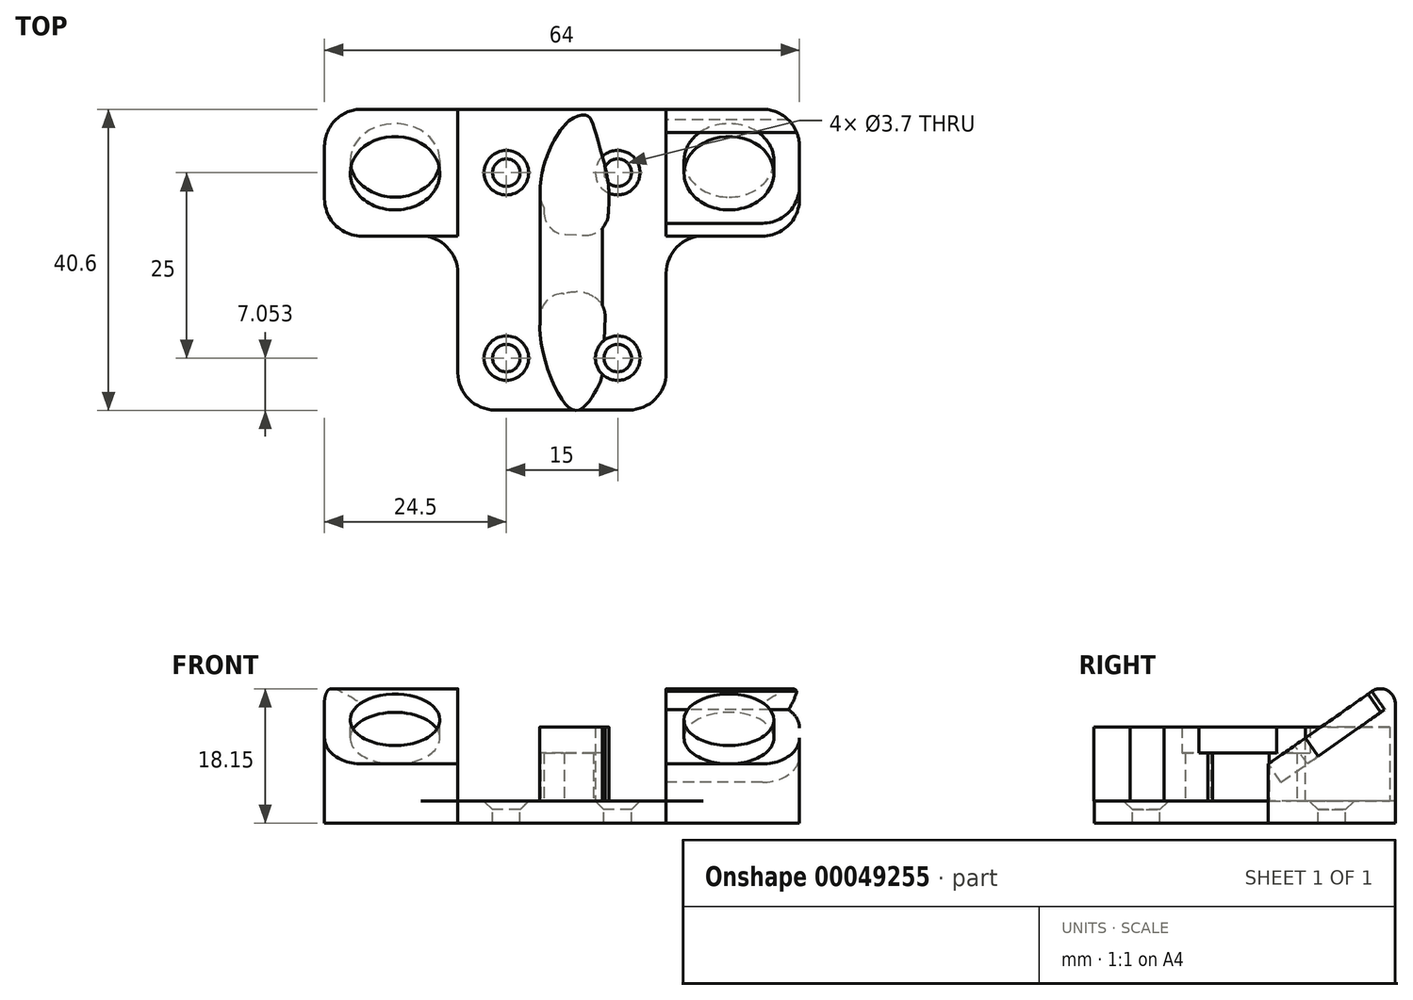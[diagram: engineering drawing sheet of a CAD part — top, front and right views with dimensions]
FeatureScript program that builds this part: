
annotation { "Feature Type Name" : "Feature", "Feature Type Description" : "" }
export const myFeature = defineFeature(function(context is Context, id is Id, definition is map)
    precondition{}
    {
        {
            var Q0;
            Q0=qCreatedBy(makeId("Top.planeOp"),FACE);
            var sketch = newSketch(context, id + "F0", { "sketchPlane" : qUnion([Q0])});
            skLineSegment(sketch, "E0.rect.top", {"start": v(-9.03, -25.17) * mm, "end": v(9.03, -25.17) * mm});
            skPoint(sketch, "E0.rect.middle", {"position": v(0, 0) * mm});
            skLineSegment(sketch, "E1.rect.bottom", {"start": v(27, 15.36) * mm, "end": v(-27, 15.36) * mm});
            skLineSegment(sketch, "E1.rect.top", {"start": v(27, -1.74) * mm, "end": v(19.03, -1.74) * mm});
            skLineSegment(sketch, "E1.rect.left", {"start": v(32, 15.36) * mm, "end": v(32, 15.36) * mm});
            skLineSegment(sketch, "E1.rect.right", {"start": v(-32, 10.36) * mm, "end": v(-32, 3.26) * mm});
            skPoint(sketch, "E1.rect.middle", {"position": v(0, 6.81) * mm});
            skLineSegment(sketch, "E2.trimOffspring", {"start": v(-19.03, -1.74) * mm, "end": v(-27, -1.74) * mm});
            skLineSegment(sketch, "E3", {"start": v(0, 6.81) * mm, "end": v(0, -18.19) * mm, "construction": true});
            skPoint(sketch, "E3.endSnap0", {"position": v(0, -25.17) * mm});
            skLineSegment(sketch, "E4", {"start": v(0, 6.81) * mm, "end": v(32, 6.81) * mm, "construction": true});
            skLineSegment(sketch, "E5", {"start": v(0, 6.81) * mm, "end": v(-32, 6.81) * mm, "construction": true});
            skPoint(sketch, "E6", {"position": v(7.5, 6.81) * mm});
            skLineSegment(sketch, "E7", {"start": v(7.5, 6.81) * mm, "end": v(7.5, -18.19) * mm, "construction": true});
            skPoint(sketch, "E8", {"position": v(7.5, -18.19) * mm});
            skPoint(sketch, "E9.MirrorP", {"position": v(-7.5, -18.19) * mm});
            skPoint(sketch, "E10.MirrorP", {"position": v(-7.5, 6.81) * mm});
            skCircle(sketch, "E11", {"center": v(-22.5, 6.81) * mm, "radius": 6.05 * mm, "construction": true});
            skCircle(sketch, "E12", {"center": v(22.5, 6.72) * mm, "radius": 6.05 * mm, "construction": true});
            skLineSegment(sketch, "E13", {"start": v(-7.5, 6.81) * mm, "end": v(-7.5, -18.19) * mm, "construction": true});
            skLineSegment(sketch, "E14", {"start": v(-7.5, -18.19) * mm, "end": v(7.5, -18.19) * mm, "construction": true});
            skPoint(sketch, "E15.orphan", {"position": v(0, -14.27) * mm});
            skPoint(sketch, "E16.orphan", {"position": v(0, 15.36) * mm});
            skLineSegment(sketch, "E17", {"start": v(14.03, -20.17) * mm, "end": v(14.03, -6.74) * mm});
            skLineSegment(sketch, "E18.MirrorCS", {"start": v(-14.03, -20.17) * mm, "end": v(-14.03, -6.74) * mm});
            skPoint(sketch, "E19.orphan", {"position": v(18, -25.17) * mm});
            skPoint(sketch, "E20.orphan", {"position": v(-18, -25.17) * mm});
            skLineSegment(sketch, "E21", {"start": v(14.03, -6.74) * mm, "end": v(14.03, 15.36) * mm});
            skLineSegment(sketch, "E22", {"start": v(32, -1.74) * mm, "end": v(32, -1.74) * mm});
            skLineSegment(sketch, "E23", {"start": v(32, 10.36) * mm, "end": v(32, 3.26) * mm});
            skLineSegment(sketch, "E24", {"start": v(14.03, 15.36) * mm, "end": v(14.03, 15.36) * mm});
            skLineSegment(sketch, "E25", {"start": v(-14.03, 15.36) * mm, "end": v(-14.03, 15.36) * mm});
            skLineSegment(sketch, "E26", {"start": v(-14.03, -6.74) * mm, "end": v(-14.03, 15.36) * mm});
            skLineSegment(sketch, "E27", {"start": v(-32, -1.74) * mm, "end": v(-32, -1.74) * mm});
            skLineSegment(sketch, "E28", {"start": v(-32, 15.36) * mm, "end": v(-32, 15.36) * mm});
            skArc(sketch, "E29.filletArc", {"start": v(19.03, -1.74) * mm, "mid": v(15.5, -3.2) * mm, "end": v(14.03, -6.74) * mm});
            skArc(sketch, "E30.filletArc", {"start": v(-14.03, -6.74) * mm, "mid": v(-15.5, -3.2) * mm, "end": v(-19.03, -1.74) * mm});
            skPoint(sketch, "E31.visualSharp", {"position": v(-14.03, -25.17) * mm});
            skArc(sketch, "E31.filletArc", {"start": v(-14.03, -20.17) * mm, "mid": v(-12.57, -23.7) * mm, "end": v(-9.03, -25.17) * mm});
            skPoint(sketch, "E32.visualSharp", {"position": v(14.03, -25.17) * mm});
            skArc(sketch, "E32.filletArc", {"start": v(9.03, -25.17) * mm, "mid": v(12.57, -23.7) * mm, "end": v(14.03, -20.17) * mm});
            skPoint(sketch, "E33.visualSharp", {"position": v(32, -1.74) * mm});
            skArc(sketch, "E33.filletArc", {"start": v(27, -1.74) * mm, "mid": v(30.54, -0.27) * mm, "end": v(32, 3.26) * mm});
            skPoint(sketch, "E34.visualSharp", {"position": v(32, 15.36) * mm});
            skArc(sketch, "E34.filletArc", {"start": v(32, 10.36) * mm, "mid": v(30.54, 13.9) * mm, "end": v(27, 15.36) * mm});
            skPoint(sketch, "E35.visualSharp", {"position": v(-32, 15.36) * mm});
            skArc(sketch, "E35.filletArc", {"start": v(-27, 15.36) * mm, "mid": v(-30.54, 13.9) * mm, "end": v(-32, 10.36) * mm});
            skPoint(sketch, "E36.visualSharp", {"position": v(-32, -1.74) * mm});
            skArc(sketch, "E36.filletArc", {"start": v(-32, 3.26) * mm, "mid": v(-30.54, -0.27) * mm, "end": v(-27, -1.74) * mm});
            skPoint(sketch, "E37.orphan", {"position": v(-14.03, -4.9) * mm});
            skPoint(sketch, "E38.orphan", {"position": v(14.03, -4.9) * mm});
            skLineSegment(sketch, "E39", {"start": v(-20.86, -1.74) * mm, "end": v(21.69, -1.74) * mm});
            skSolve(sketch);
        }
        {
            var Q0;
            Q0=makeQuery(id+"F0.imprint","IMPRINT",FACE,{"disambiguationData":[TD([[makeQuery(id+"F0.imprint","IMPRINT",EDGE,{"derivedFrom":sQuery(id+"F0.wireOp",EDGE,"E1.rect.right")}),1.0]])]});
            var Q1;
            Q1=makeQuery(id+"F0.imprint","IMPRINT",FACE,{"disambiguationData":[TD([[makeQuery(id+"F0.imprint","IMPRINT",EDGE,{"derivedFrom":sQuery(id+"F0.wireOp",EDGE,"E0.rect.top")}),1.0]])]});
            var Q2;
            Q2=makeQuery(id+"F0.imprint","IMPRINT",FACE,{"disambiguationData":[TD([[makeQuery(id+"F0.imprint","IMPRINT",EDGE,{"derivedFrom":sQuery(id+"F0.wireOp",EDGE,"E1.rect.top")}),-1.0]])]});
            var Q3;
            {var subQ0=sQuery(id+"F0.wireOp",EDGE,"E21");var subQ1=sQuery(id+"F0.wireOp",EDGE,"E1.rect.bottom");var subQ2=makeQuery(id+"F0.imprint","INTERSECT",VERTEX,{"derivedFrom":[subQ1,subQ0]});Q3=makeQuery(id+"F0.imprint","IMPRINT",FACE,{"disambiguationData":[TD([[makeQuery(id+"F0.imprint","IMPRINT",EDGE,{"disambiguationData":[TD([[subQ2,-1.0]])],"derivedFrom":subQ1}),1.0]])]});}
            var Q4;
            {var subQ0=sQuery(id+"F0.wireOp",EDGE,"E30.filletArc");Q4=makeQuery(id+"F0.imprint","IMPRINT",FACE,{"disambiguationData":[TD([[makeQuery(id+"F0.imprint","IMPRINT",EDGE,{"derivedFrom":subQ0}),-1.0]])]});}
            var Q5;
            {var subQ0=sQuery(id+"F0.wireOp",EDGE,"E29.filletArc");Q5=makeQuery(id+"F0.imprint","IMPRINT",FACE,{"disambiguationData":[TD([[makeQuery(id+"F0.imprint","IMPRINT",EDGE,{"derivedFrom":subQ0}),-1.0]])]});}
            extrude(context, id + "F1", {"entities" : qUnion([Q0, Q1, Q2, Q3, Q4, Q5]), "depth" : 3 * mm});
        }
        {
            var Q0;
            Q0=qCreatedBy(makeId("Right.planeOp"),FACE);
            var sketch = newSketch(context, id + "F2", { "sketchPlane" : qUnion([Q0])});
            skLineSegment(sketch, "E40.0", {"start": v(-1.74, 3) * mm, "end": v(-1.74, 0) * mm});
            skLineSegment(sketch, "E41.0", {"start": v(15.36, 3) * mm, "end": v(15.36, 0) * mm});
            skLineSegment(sketch, "E42", {"start": v(-1.74, 3) * mm, "end": v(15.36, 3) * mm});
            skLineSegment(sketch, "E43", {"start": v(15.36, 3) * mm, "end": v(15.36, 16.15) * mm});
            skLineSegment(sketch, "E44", {"start": v(-1.74, 3) * mm, "end": v(-1.74, 8) * mm});
            skLineSegment(sketch, "E45", {"start": v(-1.74, 8) * mm, "end": v(12.22, 17.8) * mm});
            skPoint(sketch, "E46.visualSharp", {"position": v(15.36, 20) * mm});
            skArc(sketch, "E46.filletArc", {"start": v(15.36, 16.15) * mm, "mid": v(14.29, 17.93) * mm, "end": v(12.22, 17.8) * mm});
            skSolve(sketch);
        }
        {
            var Q0;
            Q0=makeQuery(id+"F2.imprint","IMPRINT",FACE,{"disambiguationData":[TD([[makeQuery(id+"F2.imprint","IMPRINT",EDGE,{"derivedFrom":sQuery(id+"F2.wireOp",EDGE,"E42")}),1.0]])]});
            var Q1;
            Q1=makeQuery(id+"F1.opExtrude","SWEPT_FACE",FACE,{"disambiguationData":[OSD([sQuery(id+"F0.wireOp",EDGE,"E23")])]});
            var Q2;
            Q2=makeQuery(id+"F1.opExtrude","SWEPT_FACE",FACE,{"disambiguationData":[OSD([sQuery(id+"F0.wireOp",EDGE,"E1.rect.right")])]});
            extrude(context, id + "F3", {"entities" : qUnion([Q0]), "operationType" : NewBodyOperationType.ADD, "endBound" : BoundingType.UP_TO_SURFACE, "endBoundEntityFace" : qUnion([Q1]), "depth" : 25 * mm, "hasSecondDirection" : true, "secondDirectionBound" : SecondDirectionBoundingType.UP_TO_SURFACE, "secondDirectionOppositeDirection" : true, "secondDirectionBoundEntityFace" : qUnion([Q2]), "secondDirectionDepth" : 25 * mm});
        }
        {
            var Q0;
            {var subQ1=sQuery(id+"F2.wireOp",EDGE,"E42");Q0=makeQuery(id+"F3.boolean.opBoolean","SPLIT",FACE,{"disambiguationData":[TD([makeQuery(id+"F1.opExtrude","SWEPT_FACE",FACE,{"disambiguationData":[OSD([sQuery(id+"F0.wireOp",EDGE,"E35.filletArc")])]})])],"derivedFrom":makeQuery(id+"F3.opExtrude","SWEPT_FACE",FACE,{"disambiguationData":[OSD([subQ1])]})});}
            var Q1;
            {var subQ2=sQuery(id+"F2.wireOp",EDGE,"E42");Q1=makeQuery(id+"F3.boolean.opBoolean","SPLIT",FACE,{"disambiguationData":[TD([makeQuery(id+"F1.opExtrude","SWEPT_FACE",FACE,{"disambiguationData":[OSD([sQuery(id+"F0.wireOp",EDGE,"E36.filletArc")])]})])],"derivedFrom":makeQuery(id+"F3.opExtrude","SWEPT_FACE",FACE,{"disambiguationData":[OSD([subQ2])]})});}
            var Q2;
            {var subQ2=sQuery(id+"F2.wireOp",EDGE,"E42");Q2=makeQuery(id+"F3.boolean.opBoolean","SPLIT",FACE,{"disambiguationData":[TD([makeQuery(id+"F1.opExtrude","SWEPT_FACE",FACE,{"disambiguationData":[OSD([sQuery(id+"F0.wireOp",EDGE,"E33.filletArc")])]})])],"derivedFrom":makeQuery(id+"F3.opExtrude","SWEPT_FACE",FACE,{"disambiguationData":[OSD([subQ2])]})});}
            var Q3;
            {var subQ1=sQuery(id+"F2.wireOp",EDGE,"E42");Q3=makeQuery(id+"F3.boolean.opBoolean","SPLIT",FACE,{"disambiguationData":[TD([makeQuery(id+"F1.opExtrude","SWEPT_FACE",FACE,{"disambiguationData":[OSD([sQuery(id+"F0.wireOp",EDGE,"E34.filletArc")])]})])],"derivedFrom":makeQuery(id+"F3.opExtrude","SWEPT_FACE",FACE,{"disambiguationData":[OSD([subQ1])]})});}
            extrude(context, id + "F4", {"entities" : qUnion([Q0, Q1, Q2, Q3]), "operationType" : NewBodyOperationType.REMOVE, "oppositeDirection" : true, "depth" : 25 * mm});
        }
        {
            var Q0;
            Q0=makeQuery(id+"F3.opExtrude","SWEPT_FACE",FACE,{"disambiguationData":[OSD([sQuery(id+"F2.wireOp",EDGE,"E45")])]});
            var sketch = newSketch(context, id + "F5", { "sketchPlane" : qUnion([Q0])});
            skCircle(sketch, "E47", {"center": v(-22.5, 13.54) * mm, "radius": 6.05 * mm});
            skLineSegment(sketch, "E48.0", {"start": v(0, 23.81) * mm, "end": v(0, -14.89) * mm, "construction": true});
            skPoint(sketch, "E49.orphan", {"position": v(0, 5.58) * mm});
            skCircle(sketch, "E50.MirrorC", {"center": v(22.5, 13.54) * mm, "radius": 6.05 * mm});
            skLineSegment(sketch, "E51.0", {"start": v(14.03, 0) * mm, "end": v(14.03, 28.57) * mm});
            skLineSegment(sketch, "E52.0", {"start": v(-14.03, 0) * mm, "end": v(-14.03, 28.57) * mm});
            skPoint(sketch, "E53.orphan", {"position": v(-14.03, 12.58) * mm});
            skPoint(sketch, "E54.orphan", {"position": v(14.03, 12.58) * mm});
            skLineSegment(sketch, "E55", {"start": v(-14.03, 28.57) * mm, "end": v(14.09, 28.57) * mm});
            skPoint(sketch, "E56.orphan", {"position": v(14.03, -5.52) * mm});
            skPoint(sketch, "E57.orphan", {"position": v(-14.03, -5.52) * mm});
            skLineSegment(sketch, "E58", {"start": v(14.03, 0) * mm, "end": v(14.03, -5.02) * mm});
            skLineSegment(sketch, "E59", {"start": v(14.03, -5.02) * mm, "end": v(-14.03, -5.02) * mm});
            skLineSegment(sketch, "E60", {"start": v(-14.03, 0) * mm, "end": v(-14.03, -5.02) * mm});
            skSolve(sketch);
        }
        {
            var Q0;
            {var subQ0=sQuery(id+"F5.wireOp",EDGE,"E51.0");var subQ1=makeQuery(id+"F2.imprint","IMPRINT",EDGE,{"derivedFrom":sQuery(id+"F2.wireOp",EDGE,"E45")});var subQ2=makeQuery(id+"F3.opExtrude","TWEAK_EDGE",EDGE,{"derivedFrom":[makeQuery(id+"F2.imprint","IMPRINT",EDGE,{"derivedFrom":sQuery(id+"F2.wireOp",EDGE,"E44")}),subQ1]});var subQ3=makeQuery(id+"F5.imprint","INTERSECT",VERTEX,{"derivedFrom":[subQ2,subQ0]});Q0=makeQuery(id+"F5.imprint","IMPRINT",FACE,{"disambiguationData":[TD([[makeQuery(id+"F5.imprint","IMPRINT",EDGE,{"disambiguationData":[TD([[subQ3,-1.0]])],"derivedFrom":subQ0}),1.0]])]});}
            var Q1;
            {var subQ0=sQuery(id+"F5.wireOp",EDGE,"E58");Q1=makeQuery(id+"F5.imprint","IMPRINT",FACE,{"disambiguationData":[TD([[makeQuery(id+"F5.imprint","IMPRINT",EDGE,{"derivedFrom":subQ0}),-1.0]])]});}
            var Q2;
            {var subQ0=sQuery(id+"F5.wireOp",EDGE,"E55");var subQ1=sQuery(id+"F5.wireOp",EDGE,"E51.0");var subQ2=makeQuery(id+"F5.imprint","INTERSECT",VERTEX,{"derivedFrom":[subQ1,subQ0]});Q2=makeQuery(id+"F5.imprint","IMPRINT",FACE,{"disambiguationData":[TD([[makeQuery(id+"F5.imprint","IMPRINT",EDGE,{"disambiguationData":[TD([[subQ2,1.0]])],"derivedFrom":subQ0}),-1.0]])]});}
            var Q3;
            Q3=makeQuery(id+"F1.opExtrude","CAP_FACE",FACE,{"disambiguationData":[OSD([sQuery(id+"F0.wireOp",EDGE,"E0.rect.top"),sQuery(id+"F0.wireOp",EDGE,"E1.rect.bottom"),sQuery(id+"F0.wireOp",EDGE,"E1.rect.top"),sQuery(id+"F0.wireOp",EDGE,"E1.rect.right"),sQuery(id+"F0.wireOp",EDGE,"E2.trimOffspring"),sQuery(id+"F0.wireOp",EDGE,"E17"),sQuery(id+"F0.wireOp",EDGE,"E18.MirrorCS"),sQuery(id+"F0.wireOp",EDGE,"E23"),sQuery(id+"F0.wireOp",EDGE,"E29.filletArc"),sQuery(id+"F0.wireOp",EDGE,"E30.filletArc"),sQuery(id+"F0.wireOp",EDGE,"E31.filletArc"),sQuery(id+"F0.wireOp",EDGE,"E32.filletArc"),sQuery(id+"F0.wireOp",EDGE,"E33.filletArc"),sQuery(id+"F0.wireOp",EDGE,"E34.filletArc"),sQuery(id+"F0.wireOp",EDGE,"E35.filletArc"),sQuery(id+"F0.wireOp",EDGE,"E36.filletArc"),sQuery(id+"F0.wireOp",EDGE,"E39")])],"isStart":false});
            extrude(context, id + "F6", {"entities" : qUnion([Q0, Q1, Q2]), "operationType" : NewBodyOperationType.REMOVE, "endBound" : BoundingType.UP_TO_SURFACE, "oppositeDirection" : true, "endBoundEntityFace" : qUnion([Q3]), "depth" : 25 * mm});
        }
        {
            var Q0;
            Q0=makeQuery(id+"F5.imprint","IMPRINT",FACE,{"disambiguationData":[TD([[makeQuery(id+"F5.imprint","IMPRINT",EDGE,{"derivedFrom":sQuery(id+"F5.wireOp",EDGE,"E50.MirrorC")}),-1.0]])]});
            var Q1;
            Q1=makeQuery(id+"F5.imprint","IMPRINT",FACE,{"disambiguationData":[TD([[makeQuery(id+"F5.imprint","IMPRINT",EDGE,{"derivedFrom":sQuery(id+"F5.wireOp",EDGE,"E47")}),1.0]])]});
            extrude(context, id + "F7", {"entities" : qUnion([Q0, Q1]), "operationType" : NewBodyOperationType.REMOVE, "oppositeDirection" : true, "depth" : 3 * mm});
        }
        {
            var Q0;
            Q0=makeQuery(id+"F6.boolean.opBoolean","MERGE",FACE,{"derivedFrom":[makeQuery(id+"F1.opExtrude","CAP_FACE",FACE,{"disambiguationData":[OSD([sQuery(id+"F0.wireOp",EDGE,"E0.rect.top"),sQuery(id+"F0.wireOp",EDGE,"E1.rect.bottom"),sQuery(id+"F0.wireOp",EDGE,"E1.rect.top"),sQuery(id+"F0.wireOp",EDGE,"E1.rect.right"),sQuery(id+"F0.wireOp",EDGE,"E2.trimOffspring"),sQuery(id+"F0.wireOp",EDGE,"E17"),sQuery(id+"F0.wireOp",EDGE,"E18.MirrorCS"),sQuery(id+"F0.wireOp",EDGE,"E23"),sQuery(id+"F0.wireOp",EDGE,"E29.filletArc"),sQuery(id+"F0.wireOp",EDGE,"E30.filletArc"),sQuery(id+"F0.wireOp",EDGE,"E31.filletArc"),sQuery(id+"F0.wireOp",EDGE,"E32.filletArc"),sQuery(id+"F0.wireOp",EDGE,"E33.filletArc"),sQuery(id+"F0.wireOp",EDGE,"E34.filletArc"),sQuery(id+"F0.wireOp",EDGE,"E35.filletArc"),sQuery(id+"F0.wireOp",EDGE,"E36.filletArc"),sQuery(id+"F0.wireOp",EDGE,"E39")])],"isStart":false}),makeQuery(id+"F6.opExtrude","CAP_FACE",FACE,{"disambiguationData":[OSD([sQuery(id+"F5.wireOp",EDGE,"E51.0"),sQuery(id+"F5.wireOp",EDGE,"E52.0"),sQuery(id+"F5.wireOp",EDGE,"E55"),sQuery(id+"F5.wireOp",EDGE,"E58"),sQuery(id+"F5.wireOp",EDGE,"E59"),sQuery(id+"F5.wireOp",EDGE,"E60")])],"isStart":false})]});
            var sketch = newSketch(context, id + "F8", { "sketchPlane" : qUnion([Q0])});
            skLineSegment(sketch, "E61.0", {"start": v(7.5, 6.81) * mm, "end": v(7.5, -18.19) * mm, "construction": true});
            skLineSegment(sketch, "E62.0", {"start": v(-7.5, 6.81) * mm, "end": v(-7.5, -18.19) * mm, "construction": true});
            skPoint(sketch, "E63", {"position": v(7.5, -5.69) * mm});
            skLineSegment(sketch, "E64", {"start": v(7.5, -5.69) * mm, "end": v(-7.5, -5.69) * mm, "construction": true});
            skFitSpline(sketch, "E65", {"points": [v(3.44, 14.46) * mm, v(4.53, 12.17) * mm, v(6, 1.95) * mm, v(1.3, 0) * mm, v(-2.85, 3.22) * mm, v(0.62, 13.51) * mm, v(3.44, 14.46) * mm]});
            skPoint(sketch, "E66", {"position": v(6, 15.36) * mm});
            skArc(sketch, "E67", {"start": v(5.45, 9) * mm, "mid": v(4.55, 6.3) * mm, "end": v(6.32, 4.05) * mm});
            skPoint(sketch, "E68.MirrorP", {"position": v(6, -26.74) * mm});
            skPoint(sketch, "E69.trimOffspring.end.orphan", {"position": v(0, 15.36) * mm});
            skPoint(sketch, "E70.0.start.orphan", {"position": v(0, -1.74) * mm});
            skPoint(sketch, "E71.4.internal.snap0", {"position": v(0, -25.17) * mm});
            skFitSpline(sketch, "E71", {"points": [v(6.32, -15.43) * mm, v(4.76, -10.37) * mm, v(0, -9.59) * mm, v(-2.94, -13.26) * mm, v(0, -23.8) * mm, v(2.28, -25.17) * mm, v(4.46, -22.76) * mm, v(5.45, -20.38) * mm], "startDerivative": vector(-7.9, 22.48) * mm, "endDerivative": vector(4.5, 23.19) * mm});
            skLineSegment(sketch, "E72.left", {"start": v(-2.43, 2.12) * mm, "end": v(-2.44, 1.59) * mm});
            skLineSegment(sketch, "E72.right", {"start": v(6.32, 4.05) * mm, "end": v(6.24, 1.3) * mm});
            skLineSegment(sketch, "E73", {"start": v(0.43, -1.5) * mm, "end": v(3.11, -1.61) * mm});
            skLineSegment(sketch, "E74", {"start": v(0.17, -9.5) * mm, "end": v(2.86, -9.54) * mm});
            skLineSegment(sketch, "E75.trimOffspring", {"start": v(-2.87, -12.4) * mm, "end": v(-2.95, -15) * mm});
            skLineSegment(sketch, "E76.trimOffspring", {"start": v(5.8, -12.63) * mm, "end": v(5.71, -15.78) * mm});
            skPoint(sketch, "E77.visualSharp", {"position": v(-2.53, -1.38) * mm});
            skArc(sketch, "E77.filletArc", {"start": v(-2.44, 1.59) * mm, "mid": v(-1.64, -0.55) * mm, "end": v(0.43, -1.5) * mm});
            skPoint(sketch, "E78.visualSharp", {"position": v(6.14, -1.74) * mm});
            skArc(sketch, "E78.filletArc", {"start": v(3.11, -1.61) * mm, "mid": v(5.28, -0.81) * mm, "end": v(6.24, 1.3) * mm});
            skPoint(sketch, "E79.visualSharp", {"position": v(5.9, -9.59) * mm});
            skArc(sketch, "E79.filletArc", {"start": v(5.8, -12.63) * mm, "mid": v(4.98, -10.47) * mm, "end": v(2.86, -9.54) * mm});
            skPoint(sketch, "E80.visualSharp", {"position": v(-2.78, -9.45) * mm});
            skArc(sketch, "E80.filletArc", {"start": v(0.17, -9.5) * mm, "mid": v(-1.94, -10.33) * mm, "end": v(-2.87, -12.4) * mm});
            skArc(sketch, "E81", {"start": v(5.71, -15.78) * mm, "mid": v(4.5, -18.02) * mm, "end": v(5.45, -20.38) * mm});
            skSolve(sketch);
        }
        {
            var Q0;
            Q0 = qSketchRegion(id + "F8", true);
            extrude(context, id + "F9", {"entities" : qUnion([Q0]), "operationType" : NewBodyOperationType.ADD, "depth" : 10 * mm});
        }
        {
            var Q0;
            Q0=sQuery(id+"F8.wireOp",VERTEX,"E62.0.start");
            var Q1;
            Q1=sQuery(id+"F8.wireOp",VERTEX,"E62.0.end");
            var Q2;
            Q2=sQuery(id+"F8.wireOp",VERTEX,"E67.center");
            var Q3;
            Q3=sQuery(id+"F8.wireOp",VERTEX,"7a332efa-baa1-4e39-bd40-679ceab8c39f0.MirrorCS.center");
            var Q4;
            Q4=sQuery(id+"F8.wireOp",VERTEX,"E61.0.end");
            var Q5;
            Q5=makeQuery(id+"F1.opExtrude","SWEPT_BODY",BODY,{"disambiguationData":[OSD([sQuery(id+"F0.wireOp",EDGE,"E0.rect.top"),sQuery(id+"F0.wireOp",EDGE,"E1.rect.bottom"),sQuery(id+"F0.wireOp",EDGE,"E1.rect.top"),sQuery(id+"F0.wireOp",EDGE,"E1.rect.right"),sQuery(id+"F0.wireOp",EDGE,"E2.trimOffspring"),sQuery(id+"F0.wireOp",EDGE,"E17"),sQuery(id+"F0.wireOp",EDGE,"E18.MirrorCS"),sQuery(id+"F0.wireOp",EDGE,"E23"),sQuery(id+"F0.wireOp",EDGE,"E29.filletArc"),sQuery(id+"F0.wireOp",EDGE,"E30.filletArc"),sQuery(id+"F0.wireOp",EDGE,"E31.filletArc"),sQuery(id+"F0.wireOp",EDGE,"E32.filletArc"),sQuery(id+"F0.wireOp",EDGE,"E33.filletArc"),sQuery(id+"F0.wireOp",EDGE,"E34.filletArc"),sQuery(id+"F0.wireOp",EDGE,"E35.filletArc"),sQuery(id+"F0.wireOp",EDGE,"E36.filletArc"),sQuery(id+"F0.wireOp",EDGE,"E39")])]});
            hole(context, id + "F10", {"style" : HoleStyle.C_SINK, "holeDiameter" : 3.7 * mm, "cSinkDiameter" : 6 * mm, "endStyle" : HoleEndStyle.THROUGH, "locations" : qUnion([Q0, Q1, Q2, Q3, Q4]), "scope" : qUnion([Q5]), "cSinkAngle" : 90 * degree});
        }
        {
            var Q0;
            Q0=qCreatedBy(makeId("Front.planeOp"),FACE);
            var sketch = newSketch(context, id + "F11", { "sketchPlane" : qUnion([Q0])});
            skLineSegment(sketch, "E82.0.3", {"start": v(5.45, 9.5) * mm, "end": v(5.45, 13) * mm});
            skFitSpline(sketch, "E82.0.4", {"points": [v(5.46, 13) * mm, v(2.65, 13) * mm, v(-0.15, 13) * mm, v(-2.95, 13) * mm]});
            skLineSegment(sketch, "E82.0.5", {"start": v(-2.95, 13) * mm, "end": v(-2.95, 9.5) * mm});
            skPoint(sketch, "E83", {"position": v(-2.95, 9.5) * mm});
            skLineSegment(sketch, "E84", {"start": v(-2.95, 9.5) * mm, "end": v(5.45, 9.5) * mm});
            skPoint(sketch, "E82.0.0.start.orphan", {"position": v(-2.95, 3) * mm});
            skPoint(sketch, "E82.0.2.end.orphan", {"position": v(5.45, 3) * mm});
            skPoint(sketch, "E82.0.1.end.orphan", {"position": v(2.28, 3) * mm});
            skPoint(sketch, "E82.0.1.start.orphan", {"position": v(1.5, 3) * mm});
            skSolve(sketch);
        }
        {
            var Q0;
            Q0 = qSketchRegion(id + "F11", true);
            extrude(context, id + "F12", {"entities" : qUnion([Q0]), "operationType" : NewBodyOperationType.ADD, "depth" : 25 * mm});
        }
        {
            var Q0;
            {var subQ0=sQuery(id+"F11.wireOp",EDGE,"E82.0.5");var subQ1=sQuery(id+"F11.wireOp",EDGE,"E84");var subQ2=makeQuery(id+"F12.opExtrude","SWEPT_FACE",FACE,{"disambiguationData":[OSD([subQ1])]});Q0=makeQuery(id+"F12.boolean.opBoolean","SPLIT",FACE,{"disambiguationData":[TD([makeQuery(id+"F9.opExtrude","SWEPT_FACE",FACE,{"disambiguationData":[OSD([sQuery(id+"F8.wireOp",EDGE,"E71")])]}),makeQuery(id+"F9.opExtrude","SWEPT_FACE",FACE,{"disambiguationData":[OSD([sQuery(id+"F8.wireOp",EDGE,"E75.trimOffspring")])]}),makeQuery(id+"F12.opExtrude","CAP_FACE",FACE,{"disambiguationData":[OSD([sQuery(id+"F11.wireOp",EDGE,"E82.0.3"),sQuery(id+"F11.wireOp",EDGE,"E82.0.4"),subQ0,subQ1])],"isStart":false}),makeQuery(id+"F12.opExtrude","SWEPT_FACE",FACE,{"disambiguationData":[OSD([subQ0])]}),subQ2])],"derivedFrom":subQ2});}
            var Q1;
            {var subQ0=sQuery(id+"F11.wireOp",EDGE,"E84");var subQ1=sQuery(id+"F11.wireOp",EDGE,"E82.0.3");var subQ2=makeQuery(id+"F12.opExtrude","SWEPT_FACE",FACE,{"disambiguationData":[OSD([subQ0])]});Q1=makeQuery(id+"F12.boolean.opBoolean","SPLIT",FACE,{"disambiguationData":[TD([makeQuery(id+"F9.opExtrude","SWEPT_FACE",FACE,{"disambiguationData":[OSD([sQuery(id+"F8.wireOp",EDGE,"E71")])]}),makeQuery(id+"F9.opExtrude","SWEPT_FACE",FACE,{"disambiguationData":[OSD([sQuery(id+"F8.wireOp",EDGE,"E81")])]}),makeQuery(id+"F12.opExtrude","SWEPT_FACE",FACE,{"disambiguationData":[OSD([subQ1])]}),makeQuery(id+"F12.opExtrude","CAP_FACE",FACE,{"disambiguationData":[OSD([subQ1,sQuery(id+"F11.wireOp",EDGE,"E82.0.4"),sQuery(id+"F11.wireOp",EDGE,"E82.0.5"),subQ0])],"isStart":false}),subQ2])],"derivedFrom":subQ2});}
            var Q2;
            {var subQ0=makeQuery(id+"F12.opExtrude","SWEPT_FACE",FACE,{"disambiguationData":[OSD([sQuery(id+"F11.wireOp",EDGE,"E84")])]});Q2=makeQuery(id+"F12.boolean.opBoolean","SPLIT",FACE,{"disambiguationData":[TD([makeQuery(id+"F9.opExtrude","SWEPT_FACE",FACE,{"disambiguationData":[OSD([sQuery(id+"F8.wireOp",EDGE,"E71")])]}),makeQuery(id+"F9.opExtrude","SWEPT_FACE",FACE,{"disambiguationData":[OSD([sQuery(id+"F8.wireOp",EDGE,"E81")])]}),makeQuery(id+"F12.opExtrude","SWEPT_FACE",FACE,{"disambiguationData":[OSD([sQuery(id+"F11.wireOp",EDGE,"E82.0.3")])]}),subQ0])],"derivedFrom":subQ0});}
            extrude(context, id + "F13", {"entities" : qUnion([Q0, Q1, Q2]), "operationType" : NewBodyOperationType.REMOVE, "oppositeDirection" : true, "depth" : 25 * mm});
        }
        {
            var Q0;
            Q0=makeQuery(id+"F12.opExtrude","CAP_FACE",FACE,{"disambiguationData":[OSD([sQuery(id+"F11.wireOp",EDGE,"E82.0.3"),sQuery(id+"F11.wireOp",EDGE,"E82.0.4"),sQuery(id+"F11.wireOp",EDGE,"E82.0.5"),sQuery(id+"F11.wireOp",EDGE,"E84")])],"isStart":true});
            extrude(context, id + "F14", {"entities" : qUnion([Q0]), "operationType" : NewBodyOperationType.ADD, "depth" : 5 * mm});
        }
    });
